# Revit family: Haworth_BuzziCube_QuatroPouf
name_source: partatom
category: Furniture
revit_build: Autodesk Revit 2018 (Build: 20170223_1515(x64)
units: mm (PartAtom-declared; Revit-internal decimal feet)

## family parameters
Always vertical = Yes
Cut with Voids When Loaded = No
OmniClass Number = 23.40.70.14.64.21
OmniClass Title = Systems Furniture
Room Calculation Point = No
Shared = No
Work Plane-Based = No

## types (4) — shared parameters
Actual Depth = 19.69 "
Actual Height = 19.69 "
Actual Width = 71.65 "
Antiskid = Yes
Assembly Code = E2020200
Base Height Control = 0.35 "
Base Width = 72.76 "
Manufacturer = Haworth
Model = HCBZ-CBP
Outer Offset = 8.85 "
Revision Number = 1
Side Part Width = 17.69 "
Size = Verify Final Dim. w/ Haworth
Square Offset = 0.45 "
Square Pouf Width = 70.76 "
URL = http://www.haworth.com
URL - Product = https://www.haworth.com
Warranty = http://www.haworth.com
Wood Base = No
Wood Finish = Haworth _ Wood _ Collection _ Ash Natural

## per-type parameters (varying)
| type | 3D Visibility | Description | Flat | Four Squares | One Square | Sixteen Squares |
| HCBZ-CBPF-4 - Flat | No | Haworth BuzziCube - Quatro Pouf - Flat | Yes | No | No | No |
| HCBZ-CBP3-401 - One Square | Yes | Haworth BuzziCube - Quatro Pouf - One Square | No | No | Yes | No |
| HCBZ-CBP3-404 - Four Squares | Yes | Haworth BuzziCube - Quatro Pouf - Four Squares | No | Yes | No | No |
| HCBZ-CBP3-416 - Sixteen Squares | Yes | Haworth BuzziCube - Quatro Pouf - Sixteen Squares | No | No | No | Yes |

## geometry (parser evidence)
native form markers: Sweep x14
no freeform markers — native parametric forms only
